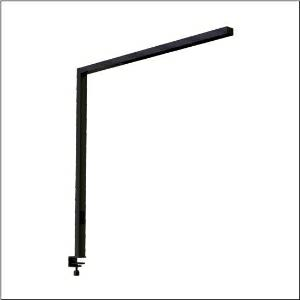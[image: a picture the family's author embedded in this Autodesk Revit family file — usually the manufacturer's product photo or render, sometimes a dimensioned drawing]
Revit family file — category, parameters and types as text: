
# Revit family: silica_r__31_desk_51my52ga4cb_9f7c
name_source: partatom
category: Lighting Fixtures
units: mm (PartAtom-declared; Revit-internal decimal feet)

## family parameters
Cut with Voids When Loaded = No
Host = Face
Light Source = No
Part Type = Normal
Room Calculation Point = No
Round Connector Dimension = Use Diameter
Shared = No

## types (1)
- Silica® 31 Desk (1 x LED, 10600 lm, 75 W, 4000K)
    Apparent Load = 75 VA
    CIE Flux Codes = 86 100 100 24 100
    Color Rendering = 80
    Color Temperature = 4000K
    Default Elevation = 1800 mm
    Description = Silica® 31 Desk, desktop luminaire, secondary optical cover: cover panel, of PMMA, light emission: direct/indirect distribution, primary light characteristic: symmetric, installation type: as desk luminaire, LED, rated luminous flux: 10.600lm, luminous efficacy: 141lm/W, light colour: 840, colour temperature: 4000K, control gear: Touchdim, daylight-dependent control, with cable with plug, mains connection: 230V, AC, 50Hz, connection cable pre-assembled, rated input power: 75W, luminaire head, of aluminium, jet black (RAL 9005), length: 1.203mm, width: 52mm, supporting column, angular, of aluminium, jet black (RAL 9005), baseplate, of steel, jet black (RAL 9005), protection rating (complete): IP20, insulation class (complete): insulation class I (protective earthing), certification: CE, permissible operating ambient temperature: -20..+40°C, standard: EN 50419, packaging unit: 1 piece
    Height = 36 mm
    Lamp = 1 x LED
    Lamp Light Flux = 10600 lm
    Lamp Power = 75 W
    Lamp count = 1
    Length = 1203 mm
    Luminous efficacy = 141 lm/W
    Manufacturer = Siteco
    ModVariant = No
    Model = 51MY52GA4CB
    Mounting Place = Floor
    Mounting Type = Freestanding
    Number of Poles = 1
    OnlyDefault = Yes
    Power Factor = 1
    Product Name = Silica® 31 Desk
    Product group = desktop luminaire
    ProductGroupID = 1303
    Protection Class = Protection class I
    Protection Degree = IP 20
    RLX_Detail_Level = 1
    RLX_Emergency_Light_Flux = 0 lm
    RLX_Emergency_Type = 0
    RLX_Emergency_Type_DB = No
    RlxData = <blob elided: 19133 chars, md5=418d7604>
    Socket = socket
    Standby Power = 0 W
    System Light Flux = 10600 lm
    System Power = 75 W
    Type Comments = Product without accessories
    Type Image = l_1275329.jpg
    URL = http://relux.com
    VarID = ---
    Voltage = 0 V
    Weight = 0.00 kg
    Width = 52 mm  [stored 0.170604 ft]

note: [stored X ft] marks values corroborated as IEEE doubles in the binary element streams (Revit-internal decimal feet)

## geometry (parser evidence)
native form markers: Blend x4, Sweep x16
no freeform markers — native parametric forms only
